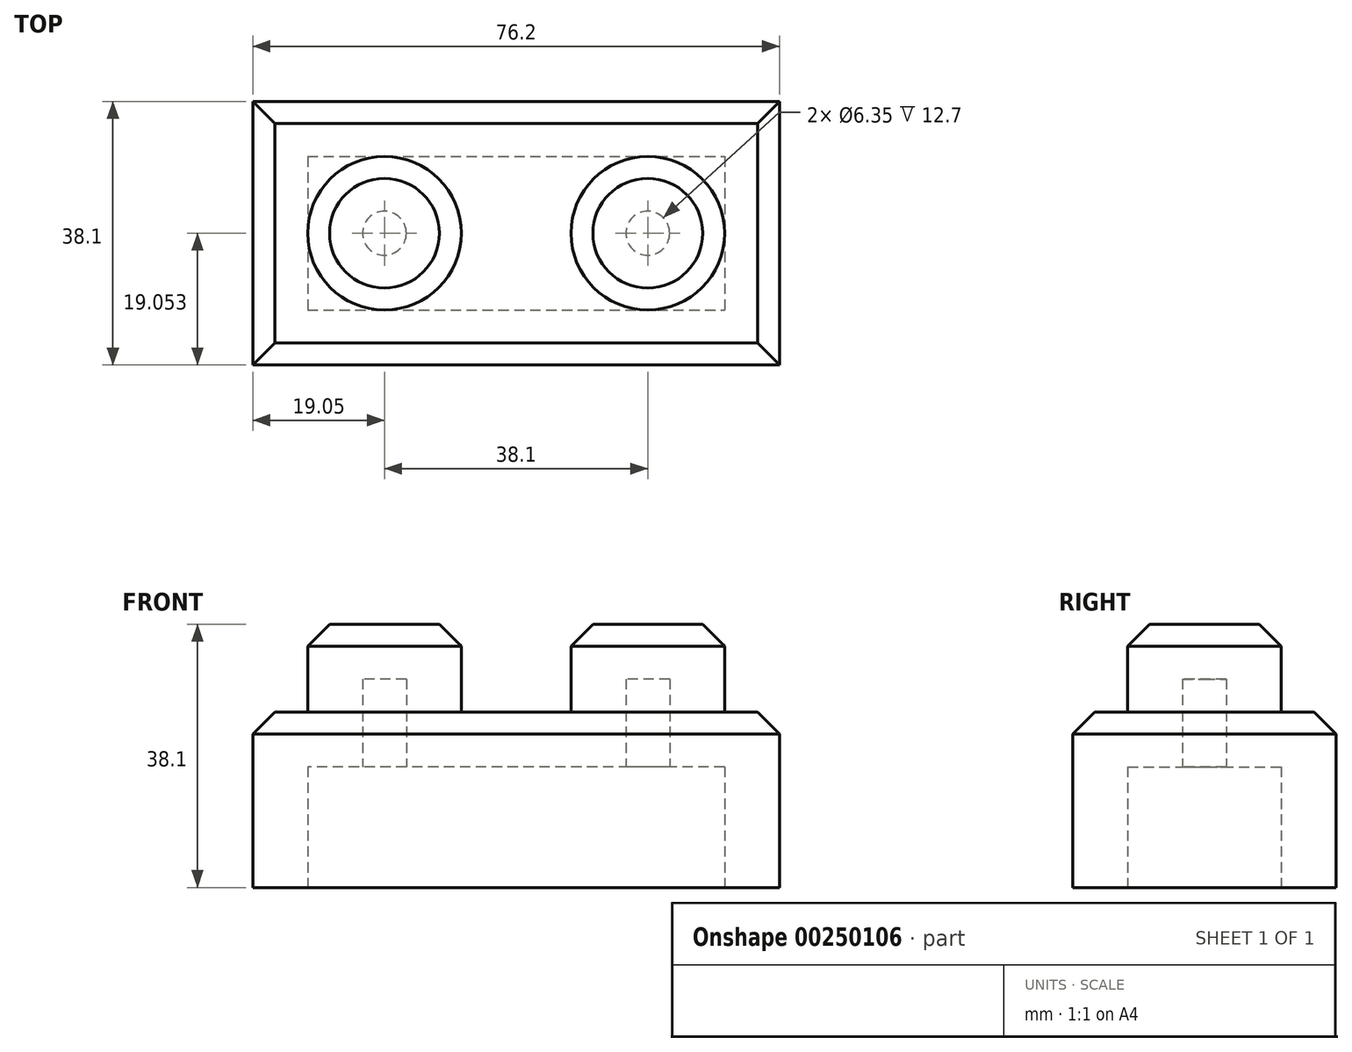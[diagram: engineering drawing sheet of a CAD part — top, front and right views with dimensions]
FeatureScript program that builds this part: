
annotation { "Feature Type Name" : "Feature", "Feature Type Description" : "" }
export const myFeature = defineFeature(function(context is Context, id is Id, definition is map)
    precondition{}
    {
        {
            var Q0;
            Q0=qCreatedBy(makeId("Top.planeOp"),FACE);
            var sketch = newSketch(context, id + "F0", { "sketchPlane" : qUnion([Q0])});
            skLineSegment(sketch, "E0.bottom", {"start": v(-76.2, 22.66) * mm, "end": v(0, 22.66) * mm});
            skLineSegment(sketch, "E0.top", {"start": v(-76.2, -15.44) * mm, "end": v(0, -15.44) * mm});
            skLineSegment(sketch, "E0.left", {"start": v(-76.2, 22.66) * mm, "end": v(-76.2, -15.44) * mm});
            skLineSegment(sketch, "E0.right", {"start": v(0, 22.66) * mm, "end": v(0, -15.44) * mm});
            skSolve(sketch);
        }
        {
            var Q0;
            Q0 = qSketchRegion(id + "F0", true);
            extrude(context, id + "F1", {"entities" : qUnion([Q0]), "depth" : 25.4 * mm});
        }
        {
            var Q0;
            Q0=makeQuery(id+"F1.opExtrude","CAP_FACE",FACE,{"disambiguationData":[OSD([sQuery(id+"F0.wireOp",EDGE,"E0.bottom"),sQuery(id+"F0.wireOp",EDGE,"E0.top"),sQuery(id+"F0.wireOp",EDGE,"E0.left"),sQuery(id+"F0.wireOp",EDGE,"E0.right")])],"isStart":false});
            var sketch = newSketch(context, id + "F2", { "sketchPlane" : qUnion([Q0])});
            skCircle(sketch, "E1", {"center": v(-57.15, 3.61) * mm, "radius": 11.11 * mm});
            skCircle(sketch, "E2", {"center": v(-19.05, 3.61) * mm, "radius": 11.11 * mm});
            skSolve(sketch);
        }
        {
            var Q0;
            Q0 = qSketchRegion(id + "F2", true);
            extrude(context, id + "F3", {"entities" : qUnion([Q0]), "operationType" : NewBodyOperationType.ADD, "depth" : 12.7 * mm});
        }
        {
            var Q0;
            Q0=makeQuery(id+"F3.opExtrude","CAP_EDGE",EDGE,{"disambiguationData":[OSD([sQuery(id+"F2.wireOp",EDGE,"E1")])],"isStart":false});
            var Q1;
            Q1=makeQuery(id+"F3.opExtrude","CAP_EDGE",EDGE,{"disambiguationData":[OSD([sQuery(id+"F2.wireOp",EDGE,"E2")])],"isStart":false});
            var Q2;
            Q2=makeQuery(id+"F1.opExtrude","CAP_EDGE",EDGE,{"disambiguationData":[OSD([sQuery(id+"F0.wireOp",EDGE,"E0.top")])],"isStart":false});
            var Q3;
            Q3=makeQuery(id+"F1.opExtrude","CAP_EDGE",EDGE,{"disambiguationData":[OSD([sQuery(id+"F0.wireOp",EDGE,"E0.right")])],"isStart":false});
            var Q4;
            Q4=makeQuery(id+"F1.opExtrude","CAP_EDGE",EDGE,{"disambiguationData":[OSD([sQuery(id+"F0.wireOp",EDGE,"E0.bottom")])],"isStart":false});
            var Q5;
            Q5=makeQuery(id+"F1.opExtrude","CAP_EDGE",EDGE,{"disambiguationData":[OSD([sQuery(id+"F0.wireOp",EDGE,"E0.left")])],"isStart":false});
            chamfer(context, id + "F4", {"entities" : qUnion([Q0, Q1, Q2, Q3, Q4, Q5]), "chamferType" : ChamferType.OFFSET_ANGLE, "width" : 3.17 * mm, "oppositeDirection" : false, "angle" : 45 * degree, "tangentPropagation" : true});
        }
        {
            var Q0;
            Q0=makeQuery(id+"F1.opExtrude","CAP_FACE",FACE,{"disambiguationData":[OSD([sQuery(id+"F0.wireOp",EDGE,"E0.bottom"),sQuery(id+"F0.wireOp",EDGE,"E0.top"),sQuery(id+"F0.wireOp",EDGE,"E0.left"),sQuery(id+"F0.wireOp",EDGE,"E0.right")])],"isStart":true});
            shell(context, id + "F5", {"entities" : qUnion([Q0]), "thickness" : 7.94 * mm});
        }
    });
